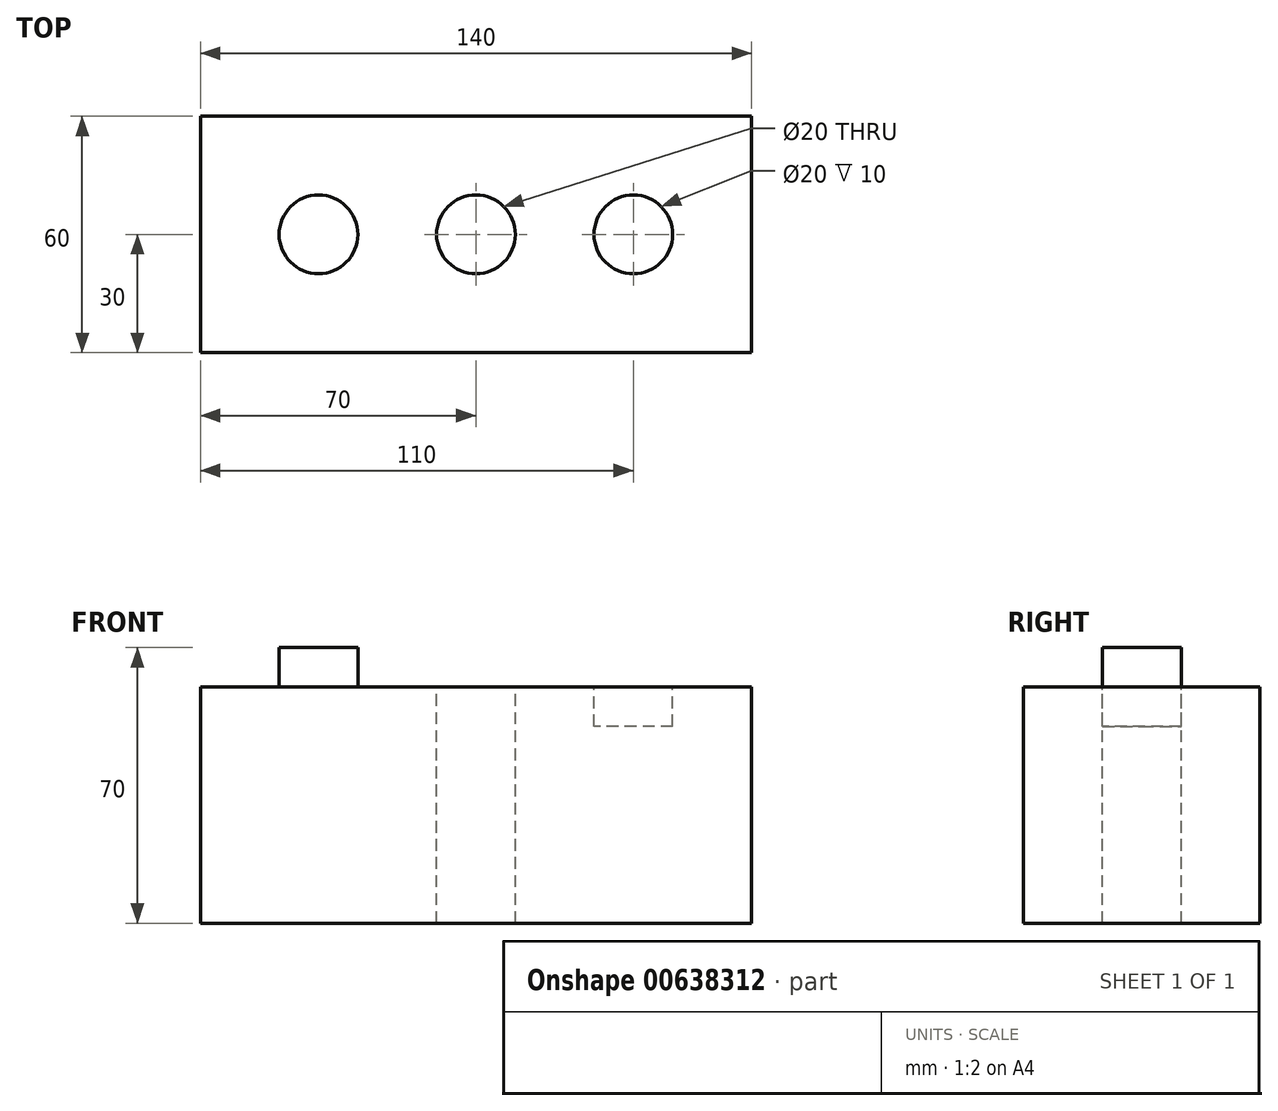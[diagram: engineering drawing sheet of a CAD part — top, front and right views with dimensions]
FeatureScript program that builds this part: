
annotation { "Feature Type Name" : "Feature", "Feature Type Description" : "" }
export const myFeature = defineFeature(function(context is Context, id is Id, definition is map)
    precondition{}
    {
        {
            var Q0;
            Q0=qCreatedBy(makeId("Top.planeOp"),FACE);
            var sketch = newSketch(context, id + "F0", { "sketchPlane" : qUnion([Q0])});
            skLineSegment(sketch, "E0.bottom", {"start": v(-70, 30) * mm, "end": v(70, 30) * mm});
            skLineSegment(sketch, "E0.top", {"start": v(-70, -30) * mm, "end": v(70, -30) * mm});
            skLineSegment(sketch, "E0.left", {"start": v(-70, 30) * mm, "end": v(-70, -30) * mm});
            skLineSegment(sketch, "E0.right", {"start": v(70, 30) * mm, "end": v(70, -30) * mm});
            skPoint(sketch, "E0.middle", {"position": v(0, 0) * mm});
            skSolve(sketch);
        }
        {
            var Q0;
            Q0 = qSketchRegion(id + "F0", true);
            extrude(context, id + "F1", {"entities" : qUnion([Q0]), "depth" : 60 * mm, "offsetDistance" : 25 * mm});
        }
        {
            var Q0;
            Q0=makeQuery(id+"F1.opExtrude","CAP_FACE",FACE,{"disambiguationData":[OSD([sQuery(id+"F0.wireOp",EDGE,"E0.bottom"),sQuery(id+"F0.wireOp",EDGE,"E0.top"),sQuery(id+"F0.wireOp",EDGE,"E0.left"),sQuery(id+"F0.wireOp",EDGE,"E0.right")])],"isStart":false});
            var sketch = newSketch(context, id + "F2", { "sketchPlane" : qUnion([Q0])});
            skSolve(sketch);
        }
        {
            var Q0;
            Q0=makeQuery(id+"F2.imprint","IMPRINT",FACE,{"disambiguationData":[TD([[makeQuery(id+"F2.imprint","IMPRINT",EDGE,{"derivedFrom":makeQuery(id+"F1.opExtrude","CAP_EDGE",EDGE,{"disambiguationData":[OSD([sQuery(id+"F0.wireOp",EDGE,"E0.bottom")])],"isStart":false})}),-1.0]])]});
            var sketch = newSketch(context, id + "F3", { "sketchPlane" : qUnion([Q0])});
            skCircle(sketch, "E1", {"center": v(-40, 0) * mm, "radius": 10 * mm});
            skSolve(sketch);
        }
        {
            var Q0;
            Q0=makeQuery(id+"F2.imprint","IMPRINT",FACE,{"disambiguationData":[TD([[makeQuery(id+"F2.imprint","IMPRINT",EDGE,{"derivedFrom":makeQuery(id+"F1.opExtrude","CAP_EDGE",EDGE,{"disambiguationData":[OSD([sQuery(id+"F0.wireOp",EDGE,"E0.bottom")])],"isStart":false})}),-1.0]])]});
            var sketch = newSketch(context, id + "F4", { "sketchPlane" : qUnion([Q0])});
            skCircle(sketch, "E2", {"center": v(0, 0) * mm, "radius": 10 * mm});
            skSolve(sketch);
        }
        {
            var Q0;
            Q0=makeQuery(id+"F2.imprint","IMPRINT",FACE,{"disambiguationData":[TD([[makeQuery(id+"F2.imprint","IMPRINT",EDGE,{"derivedFrom":makeQuery(id+"F1.opExtrude","CAP_EDGE",EDGE,{"disambiguationData":[OSD([sQuery(id+"F0.wireOp",EDGE,"E0.bottom")])],"isStart":false})}),-1.0]])]});
            var sketch = newSketch(context, id + "F5", { "sketchPlane" : qUnion([Q0])});
            skCircle(sketch, "E3", {"center": v(40, 0) * mm, "radius": 10 * mm});
            skSolve(sketch);
        }
        {
            var Q0;
            Q0 = qSketchRegion(id + "F3", true);
            extrude(context, id + "F6", {"entities" : qUnion([Q0]), "operationType" : NewBodyOperationType.ADD, "depth" : 10 * mm, "offsetDistance" : 25 * mm});
        }
        {
            var Q0;
            Q0 = qSketchRegion(id + "F4", true);
            extrude(context, id + "F7", {"entities" : qUnion([Q0]), "operationType" : NewBodyOperationType.REMOVE, "oppositeDirection" : true, "depth" : 114.6 * mm, "offsetDistance" : 25 * mm});
        }
        {
            var Q0;
            Q0 = qSketchRegion(id + "F5", true);
            extrude(context, id + "F8", {"entities" : qUnion([Q0]), "operationType" : NewBodyOperationType.REMOVE, "oppositeDirection" : true, "depth" : 10 * mm, "offsetDistance" : 25 * mm});
        }
    });
